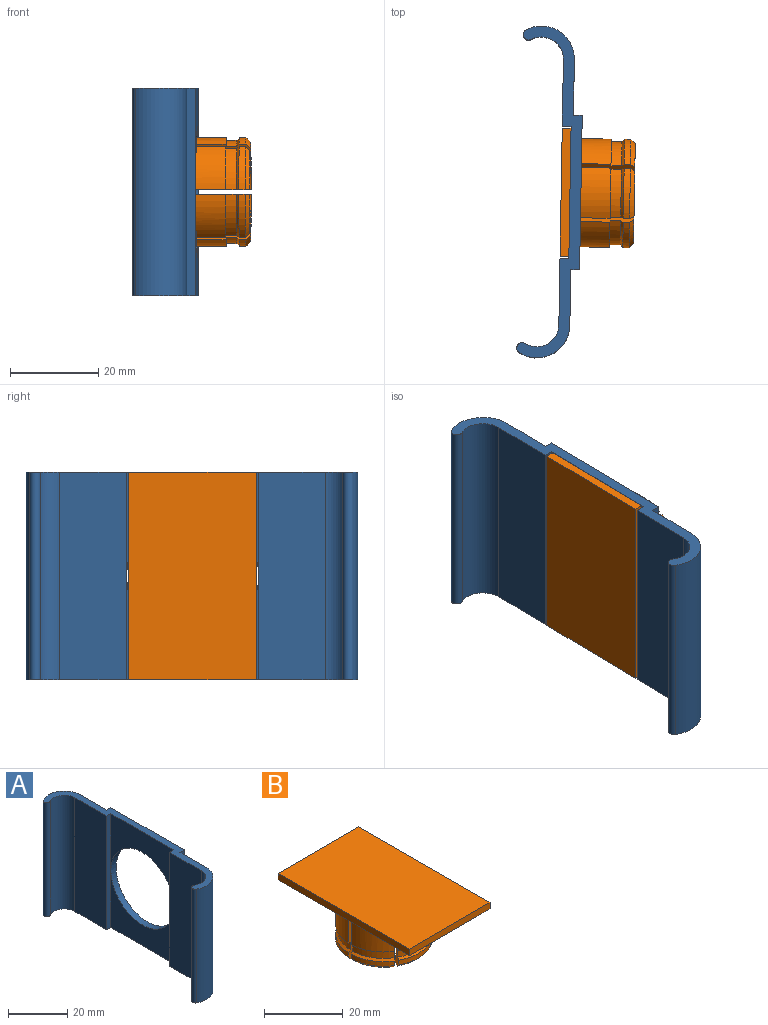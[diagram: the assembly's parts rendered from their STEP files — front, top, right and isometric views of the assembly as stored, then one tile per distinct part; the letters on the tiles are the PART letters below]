
ASSEMBLY  parts=2 mates=1
PART A: 20 faces, bbox 14x75.3x47 mm
  f0: plane 30x23.5mm, normal (-1,0,0), area 351.6mm2, adj f1,f11,f13,f17
  f1: plane 75.28x13.95mm, normal (0,0,-1), area 230mm2, adj f0,f3,f4,f5,f6,f7,f8,f9
  f2: plane 75.28x13.95mm, normal (0,0,1), area 230mm2, adj f3,f4,f5,f6,f7,f8,f9,f10
  f3: plane 47x12.66mm, normal (1,0,0), area 595mm2, adj f1,f2,f4,f9
  f4: plane 47x2mm, normal (0,-1,0), area 94mm2, adj f1,f2,f3,f5
  f5: plane 47x34.98mm, normal (1,0,0), area 937.2mm2, adj f1,f2,f4,f6,f17
  f6: plane 47x2mm, normal (0,1,0), area 94mm2, adj f1,f2,f5,f7
  f7: plane 47x12.66mm, normal (1,0,0), area 595mm2, adj f1,f2,f6,f8
  f8: cylinder r=7.49mm len=47mm, axis (0,0,1), area 728.1mm2, adj f1,f2,f7,f18
  f9: cylinder r=7.49mm len=47mm, axis (0,0,1), area 743.7mm2, adj f1,f2,f3,f19
  f10: plane 47x15.15mm, normal (-1,0,0), area 712mm2, adj f1,f2,f11,f16
  f11: plane 47x2mm, normal (0,1,0), area 94mm2, adj f0,f1,f2,f10,f12
  f12: plane 30x23.5mm, normal (-1,0,0), area 351.6mm2, adj f2,f11,f13,f17
  f13: plane 47x2mm, normal (0,-1,0), area 94mm2, adj f0,f1,f2,f12,f14
  f14: plane 47x15.15mm, normal (-1,0,0), area 712mm2, adj f1,f2,f13,f15
  f15: cylinder r=5mm len=47mm, axis (0,0,1), area 486mm2, adj f1,f2,f14,f18
  f16: cylinder r=5mm len=47mm, axis (0,0,1), area 496.4mm2, adj f1,f2,f10,f19
  f17: cylinder r=15mm len=30mm, axis (-1,0,0), area 234.7mm2, adj f0,f5,f12
  f18: cylinder r=1.25mm len=47mm, axis (0,0,1), area 183.8mm2, adj f1,f2,f8,f15
  f19: cylinder r=1.25mm len=47mm, axis (0,0,1), area 183.8mm2, adj f1,f2,f9,f16
PART B: 79 faces, bbox 29.1x47.1x16.7 mm
  f0: sphere r=10mm, area 79.2mm2, adj f6,f37,f61,f64
  f1: sphere r=10mm, area 79.2mm2, adj f7,f38,f58,f62
  f2: sphere r=10mm, area 79.2mm2, adj f8,f39,f55,f59
  f3: sphere r=10mm, area 79.2mm2, adj f9,f40,f53,f56
  f4: sphere r=10mm, area 79.2mm2, adj f10,f41,f50,f52
  f5: sphere r=10mm, area 79.2mm2, adj f11,f36,f49,f65
  f6: plane 9.02x6.32mm, normal (0,0,-1), area 21.5mm2, adj f0,f61,f64,f70
  f7: plane 9.02x6.32mm, normal (0,0,-1), area 21.5mm2, adj f1,f58,f62,f71
  f8: plane 10.41x3.2mm, normal (0,0,-1), area 21.5mm2, adj f2,f55,f59,f72
  f9: plane 9.02x6.32mm, normal (0,0,-1), area 21.5mm2, adj f3,f53,f56,f67
  f10: plane 9.02x6.32mm, normal (0,0,-1), area 21.5mm2, adj f4,f50,f52,f68
  f11: plane 10.41x3.2mm, normal (0,0,-1), area 21.5mm2, adj f5,f49,f65,f69
  f12: cylinder r=12.29mm len=11.41mm, axis (0,0,-1), area 16.9mm2, adj f49,f65,f69,f74
  f13: cylinder r=12.29mm len=9.88mm, axis (0,0,-1), area 16.9mm2, adj f61,f64,f70,f73
  f14: cylinder r=12.29mm len=9.88mm, axis (0,0,-1), area 16.9mm2, adj f58,f62,f71,f77
  f15: cylinder r=12.29mm len=11.41mm, axis (0,0,-1), area 16.9mm2, adj f55,f59,f72,f78
  f16: cylinder r=12.29mm len=9.88mm, axis (0,0,-1), area 16.9mm2, adj f53,f56,f67,f76
  f17: cylinder r=12.29mm len=9.88mm, axis (0,0,-1), area 16.9mm2, adj f50,f52,f68,f75
  f18: cylinder r=11.69mm len=9.36mm, axis (0,0,-1), area 27mm2, adj f24,f61,f64,f73
  f19: cylinder r=11.69mm len=9.36mm, axis (0,0,-1), area 27mm2, adj f25,f58,f62,f77
  f20: cylinder r=11.69mm len=10.81mm, axis (0,0,-1), area 27mm2, adj f26,f55,f59,f78
  f21: cylinder r=11.69mm len=9.36mm, axis (0,0,-1), area 27mm2, adj f27,f53,f56,f76
  f22: cylinder r=11.69mm len=9.36mm, axis (0,0,-1), area 27mm2, adj f28,f50,f52,f75
  f23: cylinder r=11.69mm len=10.81mm, axis (0,0,-1), area 27mm2, adj f29,f49,f65,f74
  f24: plane 9.88x6.01mm, normal (0,0,-1), area 6.9mm2, adj f18,f31,f61,f64
  f25: plane 9.88x6.01mm, normal (0,0,-1), area 6.9mm2, adj f19,f32,f58,f62
  f26: plane 11.41x1.93mm, normal (0,0,-1), area 6.9mm2, adj f20,f33,f55,f59
  f27: plane 9.88x6.01mm, normal (0,0,-1), area 6.9mm2, adj f21,f34,f53,f56
  f28: plane 9.88x6.01mm, normal (0,0,-1), area 6.9mm2, adj f22,f35,f50,f52
  f29: plane 11.41x1.93mm, normal (0,0,-1), area 6.9mm2, adj f23,f30,f49,f65
  f30: cylinder r=12.29mm len=11.41mm, axis (0,0,-1), area 109.2mm2, adj f29,f42,f49,f65
  f31: cylinder r=12.29mm len=9.88mm, axis (0,0,-1), area 109.2mm2, adj f24,f42,f61,f64
  f32: cylinder r=12.29mm len=9.88mm, axis (0,0,-1), area 109.2mm2, adj f25,f42,f58,f62
  f33: cylinder r=12.29mm len=11.41mm, axis (0,0,-1), area 109.2mm2, adj f26,f42,f55,f59
  f34: cylinder r=12.29mm len=9.88mm, axis (0,0,-1), area 109.2mm2, adj f27,f42,f53,f56
  f35: cylinder r=12.29mm len=9.88mm, axis (0,0,-1), area 109.2mm2, adj f28,f42,f50,f52
  f36: cylinder r=9.06mm len=8.18mm, axis (0,0,-1), area 52.4mm2, adj f5,f48,f49,f65
  f37: cylinder r=9.06mm len=7.09mm, axis (0,0,-1), area 52.4mm2, adj f0,f48,f61,f64
  f38: cylinder r=9.06mm len=7.09mm, axis (0,0,-1), area 52.4mm2, adj f1,f48,f58,f62
  f39: cylinder r=9.06mm len=8.18mm, axis (0,0,-1), area 52.4mm2, adj f2,f48,f55,f59
  f40: cylinder r=9.06mm len=7.09mm, axis (0,0,-1), area 52.4mm2, adj f3,f48,f53,f56
  f41: cylinder r=9.06mm len=7.09mm, axis (0,0,-1), area 52.4mm2, adj f4,f48,f50,f52
  f42: plane 47.02x29.02mm, normal (0,0,-1), area 888.5mm2, adj f30,f31,f32,f33,f34,f35,f44,f45
  f43: plane 47x29mm, normal (0,0,1), area 1363mm2, adj f44,f45,f46,f47
  f44: plane 29x2mm, normal (0,-1,0), area 58mm2, adj f42,f43,f45,f47
  f45: plane 47x2mm, normal (-1,0,0), area 94mm2, adj f42,f43,f44,f46
  f46: plane 29x2mm, normal (0,1,0), area 58mm2, adj f42,f43,f45,f47
  f47: plane 47x2mm, normal (1,0,0), area 94mm2, adj f42,f43,f44,f46
  f48: plane 18.14x18.14mm, normal (0,0,-1), area 258.1mm2, adj f36,f37,f38,f39,f40,f41,f51,f54
  f49: plane 14.73x2.9mm, normal (0.87,0.5,0), area 39.8mm2, adj f5,f11,f12,f23,f29,f30,f36,f51
  f50: plane 14.73x2.9mm, normal (-0.87,-0.5,0), area 39.8mm2, adj f4,f10,f17,f22,f28,f35,f41,f51
  f51: plane 3.3x2.49mm, normal (0,0,-1), area 3.2mm2, adj f42,f48,f49,f50
  f52: plane 14.73x3.33mm, normal (0,1,0), area 39.7mm2, adj f4,f10,f17,f22,f28,f35,f41,f54
  f53: plane 14.73x3.33mm, normal (0,-1,0), area 39.8mm2, adj f3,f9,f16,f21,f27,f34,f40,f54
  f54: plane 3.24x1mm, normal (0,0,-1), area 3.2mm2, adj f42,f48,f52,f53
  f55: plane 14.73x2.9mm, normal (0.87,-0.5,0), area 39.8mm2, adj f2,f8,f15,f20,f26,f33,f39,f57
  f56: plane 14.73x2.9mm, normal (-0.87,0.5,0), area 39.8mm2, adj f3,f9,f16,f21,f27,f34,f40,f57
  f57: plane 3.3x2.49mm, normal (0,0,-1), area 3.2mm2, adj f42,f48,f55,f56
  f58: plane 14.73x2.9mm, normal (0.87,0.5,0), area 39.8mm2, adj f1,f7,f14,f19,f25,f32,f38,f60
  f59: plane 14.73x2.9mm, normal (-0.87,-0.5,0), area 39.8mm2, adj f2,f8,f15,f20,f26,f33,f39,f60
  f60: plane 3.3x2.49mm, normal (0,0,-1), area 3.2mm2, adj f42,f48,f58,f59
  f61: plane 14.73x3.33mm, normal (0,1,0), area 39.8mm2, adj f0,f6,f13,f18,f24,f31,f37,f63
  f62: plane 14.73x3.33mm, normal (0,-1,0), area 39.8mm2, adj f1,f7,f14,f19,f25,f32,f38,f63
  f63: plane 3.24x1mm, normal (0,0,-1), area 3.2mm2, adj f42,f48,f61,f62
  f64: plane 14.73x2.9mm, normal (0.87,-0.5,0), area 39.8mm2, adj f0,f6,f13,f18,f24,f31,f37,f66
  f65: plane 14.73x2.9mm, normal (-0.87,0.5,0), area 39.8mm2, adj f5,f11,f12,f23,f29,f30,f36,f66
  f66: plane 3.3x2.49mm, normal (0,0,-1), area 3.2mm2, adj f42,f48,f64,f65
  f67: cone r=11.29mm half-angle=45deg, axis (0,0,1), area 16mm2, adj f9,f16,f53,f56
  f68: cone r=11.29mm half-angle=45deg, axis (0,0,1), area 16mm2, adj f10,f17,f50,f52
  f69: cone r=11.29mm half-angle=45deg, axis (0,0,1), area 16mm2, adj f11,f12,f49,f65
  f70: cone r=11.29mm half-angle=45deg, axis (0,0,1), area 16mm2, adj f6,f13,f61,f64
  f71: cone r=11.29mm half-angle=45deg, axis (0,0,1), area 16mm2, adj f7,f14,f58,f62
  f72: cone r=11.29mm half-angle=45deg, axis (0,0,1), area 16mm2, adj f8,f15,f55,f59
  f73: cone r=12.29mm half-angle=45deg, axis (0,0,-1), area 9.8mm2, adj f13,f18,f61,f64
  f74: cone r=12.29mm half-angle=45deg, axis (0,0,-1), area 9.8mm2, adj f12,f23,f49,f65
  f75: cone r=12.29mm half-angle=45deg, axis (0,0,-1), area 9.8mm2, adj f17,f22,f50,f52
  f76: cone r=12.29mm half-angle=45deg, axis (0,0,-1), area 9.8mm2, adj f16,f21,f53,f56
  f77: cone r=12.29mm half-angle=45deg, axis (0,0,-1), area 9.8mm2, adj f14,f19,f58,f62
  f78: cone r=12.29mm half-angle=45deg, axis (0,0,-1), area 9.8mm2, adj f15,f20,f55,f59
PLACE A rot(axis=(0,0,-1),1deg) t=(-24.83,-6.58,1.23)mm
PLACE B rot(axis=(0.57,-0.58,-0.58),120.6deg) t=(-3.26,23.21,24.73)mm
MATE planar A.f0 <-> B.f42  axis (-1,0.02,0) through (-22.32,23.53,1.23)mm
